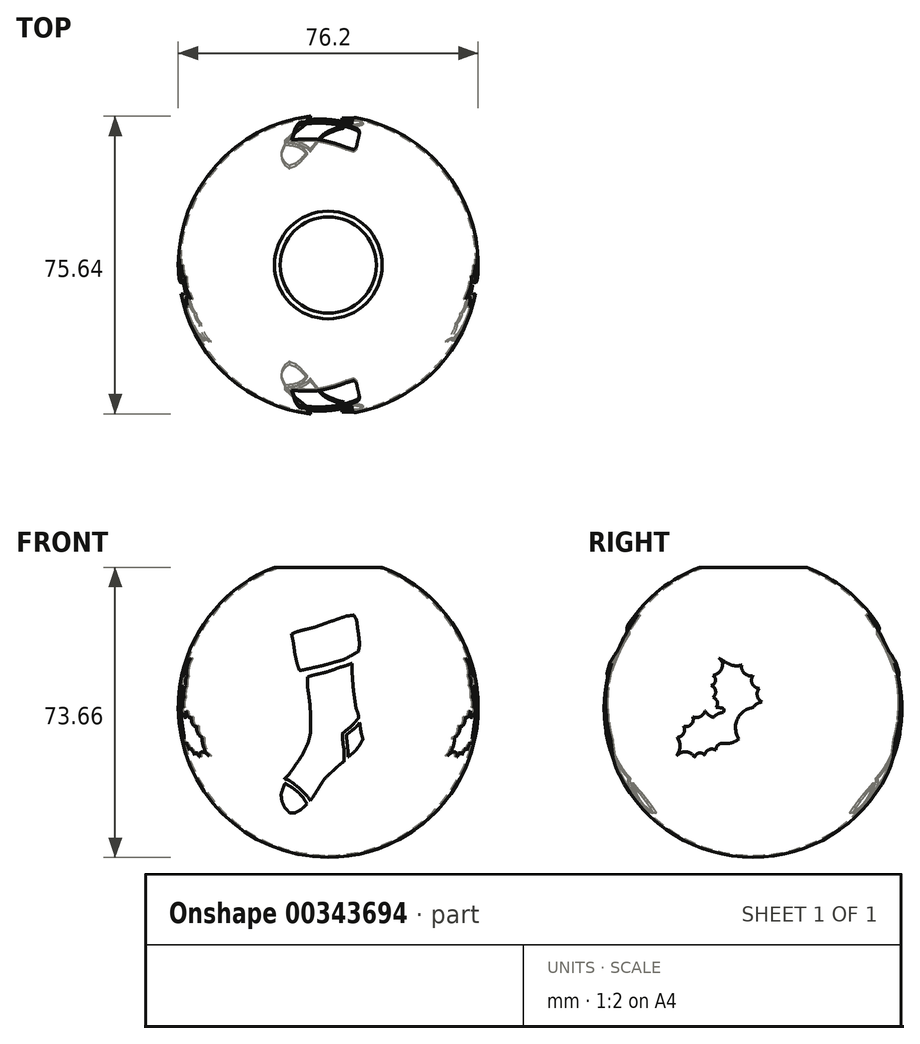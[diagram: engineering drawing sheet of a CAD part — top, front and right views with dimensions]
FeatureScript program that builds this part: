
annotation { "Feature Type Name" : "Feature", "Feature Type Description" : "" }
export const myFeature = defineFeature(function(context is Context, id is Id, definition is map)
    precondition{}
    {
        {
            var Q0;
            Q0=qCreatedBy(makeId("Front.planeOp"),FACE);
            var sketch = newSketch(context, id + "F0", { "sketchPlane" : qUnion([Q0])});
            skArc(sketch, "E0", {"start": v(0, -38.1) * mm, "mid": v(38.1, 0) * mm, "end": v(0, 38.1) * mm});
            skLineSegment(sketch, "E1", {"start": v(0, 38.1) * mm, "end": v(0, -38.1) * mm});
            skSolve(sketch);
        }
        {
            var Q0;
            Q0=makeQuery(id+"F0.imprint","IMPRINT",FACE,{"disambiguationData":[TD([[makeQuery(id+"F0.imprint","IMPRINT",EDGE,{"derivedFrom":sQuery(id+"F0.wireOp",EDGE,"E0")}),1.0]])]});
            var Q1;
            Q1=sQuery(id+"F0.wireOp",EDGE,"E1");
            revolve(context, id + "F1", {"entities" : qUnion([Q0]), "axis" : qUnion([Q1]), "revolveType" : RevolveType.FULL});
        }
        {
            var Q0;
            Q0=qCreatedBy(makeId("Top.planeOp"),FACE);
            cPlane(context, id + "F2", {"entities" : qUnion([Q0]), "cplaneType" : CPlaneType.OFFSET, "offset" : 35.56 * mm, "width" : 152.4 * mm, "height" : 152.4 * mm});
        }
        {
            var Q0;
            Q0=qCreatedBy(id+"F2.planeOp",FACE);
            var sketch = newSketch(context, id + "F3", { "sketchPlane" : qUnion([Q0])});
            skLineSegment(sketch, "E2.bottom", {"start": v(16.51, -16.51) * mm, "end": v(-16.51, -16.51) * mm});
            skLineSegment(sketch, "E2.top", {"start": v(16.5, 16.51) * mm, "end": v(-16.51, 16.51) * mm});
            skLineSegment(sketch, "E2.left", {"start": v(16.51, -16.51) * mm, "end": v(16.5, 16.51) * mm});
            skLineSegment(sketch, "E2.right", {"start": v(-16.51, -16.51) * mm, "end": v(-16.51, 16.51) * mm});
            skPoint(sketch, "E2.middle", {"position": v(0, 0) * mm});
            skSolve(sketch);
        }
        {
            var Q0;
            Q0=makeQuery(id+"F3.imprint","IMPRINT",FACE,{"disambiguationData":[TD([[makeQuery(id+"F3.imprint","IMPRINT",EDGE,{"derivedFrom":sQuery(id+"F3.wireOp",EDGE,"E2.bottom")}),-1.0]])]});
            extrude(context, id + "F4", {"entities" : qUnion([Q0]), "operationType" : NewBodyOperationType.REMOVE, "depth" : 25.4 * mm});
        }
        {
            var Q0;
            Q0=makeQuery(id+"F4.boolean.opBoolean","COPY",FACE,{"derivedFrom":makeQuery(id+"F4.opExtrude","CAP_FACE",FACE,{"disambiguationData":[OSD([sQuery(id+"F3.wireOp",EDGE,"E2.bottom"),sQuery(id+"F3.wireOp",EDGE,"E2.top"),sQuery(id+"F3.wireOp",EDGE,"E2.left"),sQuery(id+"F3.wireOp",EDGE,"E2.right")])],"isStart":true})});
            shell(context, id + "F5", {"entities" : qUnion([Q0]), "thickness" : 0.5 * mm});
        }
        {
            var Q0;
            Q0=qCreatedBy(makeId("Front.planeOp"),FACE);
            var sketch = newSketch(context, id + "F6", { "sketchPlane" : qUnion([Q0])});
            skLineSegment(sketch, "E3.bottom", {"start": v(21.25, -28.37) * mm, "end": v(-21.25, -28.37) * mm});
            skLineSegment(sketch, "E3.top", {"start": v(21.25, 28.37) * mm, "end": v(-21.25, 28.37) * mm});
            skLineSegment(sketch, "E3.left", {"start": v(21.25, -28.37) * mm, "end": v(21.25, 28.37) * mm});
            skLineSegment(sketch, "E3.right", {"start": v(-21.25, -28.37) * mm, "end": v(-21.25, 28.37) * mm});
            skPoint(sketch, "E3.middle", {"position": v(0, 0) * mm});
            skLineSegment(sketch, "E4", {"start": v(7.99, -3.87) * mm, "end": v(7.02, -5.06) * mm});
            skLineSegment(sketch, "E5", {"start": v(7.02, -5.06) * mm, "end": v(5.5, -6.3) * mm});
            skLineSegment(sketch, "E6", {"start": v(5.5, -6.3) * mm, "end": v(4.57, -7) * mm});
            skLineSegment(sketch, "E7", {"start": v(4.57, -7) * mm, "end": v(4.83, -9.38) * mm});
            skLineSegment(sketch, "E8", {"start": v(4.83, -9.38) * mm, "end": v(5.05, -11.5) * mm});
            skLineSegment(sketch, "E9", {"start": v(5.05, -11.5) * mm, "end": v(5.05, -12.65) * mm});
            skLineSegment(sketch, "E10", {"start": v(5.05, -12.65) * mm, "end": v(6.9, -11.03) * mm});
            skLineSegment(sketch, "E11", {"start": v(6.9, -11.03) * mm, "end": v(8.06, -9.46) * mm});
            skLineSegment(sketch, "E12", {"start": v(8.06, -9.46) * mm, "end": v(8.79, -8.1) * mm});
            skLineSegment(sketch, "E13", {"start": v(8.79, -8.1) * mm, "end": v(8.32, -6.34) * mm});
            skLineSegment(sketch, "E14", {"start": v(8.32, -6.34) * mm, "end": v(7.99, -3.87) * mm});
            skLineSegment(sketch, "E15", {"start": v(-11, -19.31) * mm, "end": v(-11.56, -20.72) * mm});
            skLineSegment(sketch, "E16", {"start": v(-11.56, -20.72) * mm, "end": v(-12, -22.15) * mm});
            skLineSegment(sketch, "E17", {"start": v(-12, -22.15) * mm, "end": v(-11.78, -23.85) * mm});
            skLineSegment(sketch, "E18", {"start": v(-11.78, -23.85) * mm, "end": v(-11.1, -25.37) * mm});
            skLineSegment(sketch, "E19", {"start": v(-11.1, -25.37) * mm, "end": v(-9.86, -26.76) * mm});
            skLineSegment(sketch, "E20", {"start": v(-9.86, -26.76) * mm, "end": v(-8.38, -26.76) * mm});
            skLineSegment(sketch, "E21", {"start": v(-8.38, -26.76) * mm, "end": v(-6.94, -26) * mm});
            skLineSegment(sketch, "E22", {"start": v(-6.94, -26) * mm, "end": v(-5.4, -24.55) * mm});
            skLineSegment(sketch, "E23", {"start": v(-5.4, -24.55) * mm, "end": v(-6.29, -23.06) * mm});
            skLineSegment(sketch, "E24", {"start": v(-6.29, -23.06) * mm, "end": v(-7.65, -21.58) * mm});
            skLineSegment(sketch, "E25", {"start": v(-7.65, -21.58) * mm, "end": v(-9.09, -20.42) * mm});
            skLineSegment(sketch, "E26", {"start": v(-9.09, -20.42) * mm, "end": v(-11, -19.31) * mm});
            skLineSegment(sketch, "E27", {"start": v(-9.32, 18.63) * mm, "end": v(-8.83, 16.26) * mm});
            skLineSegment(sketch, "E28", {"start": v(-8.83, 16.26) * mm, "end": v(-8.46, 13.49) * mm});
            skLineSegment(sketch, "E29", {"start": v(-8.46, 13.49) * mm, "end": v(-7.89, 11) * mm});
            skLineSegment(sketch, "E30", {"start": v(-7.89, 11) * mm, "end": v(-7.3, 9.32) * mm});
            skLineSegment(sketch, "E31", {"start": v(-7.3, 9.32) * mm, "end": v(-4.76, 9.87) * mm});
            skLineSegment(sketch, "E32", {"start": v(-4.76, 9.87) * mm, "end": v(-1.13, 10.68) * mm});
            skLineSegment(sketch, "E33", {"start": v(-1.13, 10.68) * mm, "end": v(1.48, 11.45) * mm});
            skLineSegment(sketch, "E34", {"start": v(1.48, 11.45) * mm, "end": v(4.04, 12.17) * mm});
            skLineSegment(sketch, "E35", {"start": v(4.04, 12.17) * mm, "end": v(6.16, 13.36) * mm});
            skLineSegment(sketch, "E36", {"start": v(6.16, 13.36) * mm, "end": v(7.68, 14.21) * mm});
            skLineSegment(sketch, "E37", {"start": v(7.68, 14.21) * mm, "end": v(7.99, 16.24) * mm});
            skLineSegment(sketch, "E38", {"start": v(7.99, 16.24) * mm, "end": v(7.73, 18.19) * mm});
            skLineSegment(sketch, "E39", {"start": v(7.73, 18.19) * mm, "end": v(7.41, 20.54) * mm});
            skLineSegment(sketch, "E40", {"start": v(7.41, 20.54) * mm, "end": v(7.18, 22.24) * mm});
            skLineSegment(sketch, "E41", {"start": v(7.18, 22.24) * mm, "end": v(6.51, 23.43) * mm});
            skLineSegment(sketch, "E42", {"start": v(6.51, 23.43) * mm, "end": v(4.53, 23.16) * mm});
            skLineSegment(sketch, "E43", {"start": v(4.53, 23.16) * mm, "end": v(1.92, 22.28) * mm});
            skLineSegment(sketch, "E44", {"start": v(1.92, 22.28) * mm, "end": v(-1.07, 21.23) * mm});
            skLineSegment(sketch, "E45", {"start": v(-1.07, 21.23) * mm, "end": v(-3.54, 20.32) * mm});
            skLineSegment(sketch, "E46", {"start": v(-3.54, 20.32) * mm, "end": v(-5.98, 19.74) * mm});
            skLineSegment(sketch, "E47", {"start": v(-5.98, 19.74) * mm, "end": v(-7.89, 19.24) * mm});
            skLineSegment(sketch, "E48", {"start": v(-7.89, 19.24) * mm, "end": v(-9.32, 18.63) * mm});
            skLineSegment(sketch, "E49", {"start": v(-11.16, -18.17) * mm, "end": v(-10.25, -18.4) * mm});
            skLineSegment(sketch, "E50", {"start": v(-10.25, -18.4) * mm, "end": v(-9.32, -18.94) * mm});
            skLineSegment(sketch, "E51", {"start": v(-9.32, -18.94) * mm, "end": v(-8.4, -19.68) * mm});
            skLineSegment(sketch, "E52", {"start": v(-8.4, -19.68) * mm, "end": v(-7.26, -20.6) * mm});
            skLineSegment(sketch, "E53", {"start": v(-7.26, -20.6) * mm, "end": v(-6.29, -21.58) * mm});
            skLineSegment(sketch, "E54", {"start": v(-6.29, -21.58) * mm, "end": v(-5.31, -22.56) * mm});
            skLineSegment(sketch, "E55", {"start": v(-5.31, -22.56) * mm, "end": v(-4.54, -23.7) * mm});
            skLineSegment(sketch, "E56", {"start": v(-4.54, -23.7) * mm, "end": v(-3.73, -22.56) * mm});
            skLineSegment(sketch, "E57", {"start": v(-3.73, -22.56) * mm, "end": v(-2.68, -20.89) * mm});
            skLineSegment(sketch, "E58", {"start": v(-2.68, -20.89) * mm, "end": v(-1.88, -19.57) * mm});
            skLineSegment(sketch, "E59", {"start": v(-1.88, -19.57) * mm, "end": v(-0.96, -18.16) * mm});
            skLineSegment(sketch, "E60", {"start": v(-0.96, -18.16) * mm, "end": v(0.25, -16.96) * mm});
            skLineSegment(sketch, "E61", {"start": v(0.25, -16.96) * mm, "end": v(1.32, -16.03) * mm});
            skLineSegment(sketch, "E62", {"start": v(1.32, -16.03) * mm, "end": v(2.34, -15.02) * mm});
            skLineSegment(sketch, "E63", {"start": v(2.34, -15.02) * mm, "end": v(3.5, -14.06) * mm});
            skLineSegment(sketch, "E64", {"start": v(3.5, -14.06) * mm, "end": v(4.06, -13.73) * mm});
            skLineSegment(sketch, "E65", {"start": v(4.06, -13.73) * mm, "end": v(4.06, -12.82) * mm});
            skLineSegment(sketch, "E66", {"start": v(4.06, -12.82) * mm, "end": v(4.06, -11.83) * mm});
            skLineSegment(sketch, "E67", {"start": v(4.06, -11.83) * mm, "end": v(4.06, -10.83) * mm});
            skLineSegment(sketch, "E68", {"start": v(4.06, -10.83) * mm, "end": v(3.83, -9.8) * mm});
            skLineSegment(sketch, "E69", {"start": v(3.83, -9.8) * mm, "end": v(3.67, -8.4) * mm});
            skLineSegment(sketch, "E70", {"start": v(3.67, -8.4) * mm, "end": v(3.56, -6.7) * mm});
            skLineSegment(sketch, "E71", {"start": v(3.56, -6.7) * mm, "end": v(4.57, -5.86) * mm});
            skLineSegment(sketch, "E72", {"start": v(4.57, -5.86) * mm, "end": v(5.67, -4.96) * mm});
            skLineSegment(sketch, "E73", {"start": v(5.67, -4.96) * mm, "end": v(6.5, -4.14) * mm});
            skLineSegment(sketch, "E74", {"start": v(6.5, -4.14) * mm, "end": v(7.35, -3.1) * mm});
            skLineSegment(sketch, "E75", {"start": v(7.35, -3.1) * mm, "end": v(7.76, -2.7) * mm});
            skLineSegment(sketch, "E76", {"start": v(7.76, -2.7) * mm, "end": v(7.56, -1.48) * mm});
            skLineSegment(sketch, "E77", {"start": v(7.56, -1.48) * mm, "end": v(7.05, -0.23) * mm});
            skLineSegment(sketch, "E78", {"start": v(7.05, -0.23) * mm, "end": v(6.79, 1.54) * mm});
            skLineSegment(sketch, "E79", {"start": v(6.79, 1.54) * mm, "end": v(6.56, 3.12) * mm});
            skLineSegment(sketch, "E80", {"start": v(6.56, 3.12) * mm, "end": v(6.31, 5.1) * mm});
            skLineSegment(sketch, "E81", {"start": v(6.31, 5.1) * mm, "end": v(6.18, 7.12) * mm});
            skLineSegment(sketch, "E82", {"start": v(6.18, 7.12) * mm, "end": v(6.06, 8.96) * mm});
            skLineSegment(sketch, "E83", {"start": v(6.06, 8.96) * mm, "end": v(6.06, 10.5) * mm});
            skLineSegment(sketch, "E84", {"start": v(6.06, 10.5) * mm, "end": v(6.01, 11.18) * mm});
            skLineSegment(sketch, "E85", {"start": v(6.01, 11.18) * mm, "end": v(4.57, 10.62) * mm});
            skLineSegment(sketch, "E86", {"start": v(4.57, 10.62) * mm, "end": v(2.81, 10.15) * mm});
            skLineSegment(sketch, "E87", {"start": v(2.81, 10.15) * mm, "end": v(1.27, 9.54) * mm});
            skLineSegment(sketch, "E88", {"start": v(1.27, 9.54) * mm, "end": v(-0.71, 8.9) * mm});
            skLineSegment(sketch, "E89", {"start": v(-0.71, 8.9) * mm, "end": v(-2.53, 8.46) * mm});
            skLineSegment(sketch, "E90", {"start": v(-2.53, 8.46) * mm, "end": v(-4.16, 8.1) * mm});
            skLineSegment(sketch, "E91", {"start": v(-4.16, 8.1) * mm, "end": v(-5.31, 7.72) * mm});
            skLineSegment(sketch, "E92", {"start": v(-5.31, 7.72) * mm, "end": v(-5.31, 6.24) * mm});
            skLineSegment(sketch, "E93", {"start": v(-5.31, 6.24) * mm, "end": v(-5.22, 4.9) * mm});
            skLineSegment(sketch, "E94", {"start": v(-5.22, 4.9) * mm, "end": v(-4.92, 2.96) * mm});
            skLineSegment(sketch, "E95", {"start": v(-4.92, 2.96) * mm, "end": v(-4.67, 0.9) * mm});
            skLineSegment(sketch, "E96", {"start": v(-4.67, 0.9) * mm, "end": v(-4.55, -0.96) * mm});
            skLineSegment(sketch, "E97", {"start": v(-4.55, -0.96) * mm, "end": v(-4.55, -3.08) * mm});
            skLineSegment(sketch, "E98", {"start": v(-4.55, -3.08) * mm, "end": v(-4.55, -4.42) * mm});
            skLineSegment(sketch, "E99", {"start": v(-4.55, -4.42) * mm, "end": v(-4.55, -6.7) * mm});
            skLineSegment(sketch, "E100", {"start": v(-4.55, -6.7) * mm, "end": v(-5.03, -8.73) * mm});
            skLineSegment(sketch, "E101", {"start": v(-5.03, -8.73) * mm, "end": v(-5.65, -10.16) * mm});
            skLineSegment(sketch, "E102", {"start": v(-5.65, -10.16) * mm, "end": v(-6.5, -11.91) * mm});
            skLineSegment(sketch, "E103", {"start": v(-6.5, -11.91) * mm, "end": v(-7.37, -13.3) * mm});
            skLineSegment(sketch, "E104", {"start": v(-7.37, -13.3) * mm, "end": v(-8.16, -14.42) * mm});
            skLineSegment(sketch, "E105", {"start": v(-8.16, -14.42) * mm, "end": v(-9.16, -15.9) * mm});
            skLineSegment(sketch, "E106", {"start": v(-9.16, -15.9) * mm, "end": v(-10.1, -17.22) * mm});
            skLineSegment(sketch, "E107", {"start": v(-10.1, -17.22) * mm, "end": v(-11.16, -18.17) * mm});
            skArc(sketch, "E108", {"start": v(8.32, 23.55) * mm, "mid": v(7.94, 24.06) * mm, "end": v(7.37, 24.35) * mm});
            skLineSegment(sketch, "E109", {"start": v(8.32, 23.55) * mm, "end": v(8.48, 22.17) * mm});
            skLineSegment(sketch, "E110", {"start": v(8.48, 22.17) * mm, "end": v(8.6, 20.99) * mm});
            skLineSegment(sketch, "E111", {"start": v(8.6, 20.99) * mm, "end": v(8.72, 19.86) * mm});
            skLineSegment(sketch, "E112", {"start": v(8.72, 19.86) * mm, "end": v(9.04, 18.6) * mm});
            skLineSegment(sketch, "E113", {"start": v(9.04, 18.6) * mm, "end": v(9.24, 17.76) * mm});
            skLineSegment(sketch, "E114", {"start": v(9.24, 17.76) * mm, "end": v(9.24, 17.4) * mm});
            skLineSegment(sketch, "E115", {"start": v(9.24, 17.4) * mm, "end": v(9.24, 15.65) * mm});
            skArc(sketch, "E116", {"start": v(9.05, 14.16) * mm, "mid": v(9.19, 14.9) * mm, "end": v(9.24, 15.65) * mm});
            skLineSegment(sketch, "E117", {"start": v(9.05, 14.16) * mm, "end": v(8.16, 13.16) * mm});
            skLineSegment(sketch, "E118", {"start": v(8.16, 13.16) * mm, "end": v(7.24, 12.32) * mm});
            skLineSegment(sketch, "E119", {"start": v(7.24, 12.32) * mm, "end": v(7.24, 11.36) * mm});
            skLineSegment(sketch, "E120", {"start": v(7.24, 11.36) * mm, "end": v(7.24, 10.37) * mm});
            skLineSegment(sketch, "E121", {"start": v(7.24, 10.37) * mm, "end": v(7.24, 8.7) * mm});
            skLineSegment(sketch, "E122", {"start": v(7.24, 8.7) * mm, "end": v(7.24, 6.82) * mm});
            skLineSegment(sketch, "E123", {"start": v(7.24, 6.82) * mm, "end": v(7.45, 5.06) * mm});
            skLineSegment(sketch, "E124", {"start": v(7.45, 5.06) * mm, "end": v(7.58, 3.41) * mm});
            skLineSegment(sketch, "E125", {"start": v(7.58, 3.41) * mm, "end": v(7.79, 1.83) * mm});
            skLineSegment(sketch, "E126", {"start": v(7.79, 1.83) * mm, "end": v(8.04, 0.59) * mm});
            skLineSegment(sketch, "E127", {"start": v(8.04, 0.59) * mm, "end": v(8.39, -0.63) * mm});
            skLineSegment(sketch, "E128", {"start": v(8.39, -0.63) * mm, "end": v(8.78, -2.4) * mm});
            skLineSegment(sketch, "E129", {"start": v(8.78, -2.4) * mm, "end": v(9.05, -4.12) * mm});
            skArc(sketch, "E130", {"start": v(9.34, -6.35) * mm, "mid": v(9.21, -5.23) * mm, "end": v(9.05, -4.12) * mm});
            skLineSegment(sketch, "E131", {"start": v(9.34, -6.35) * mm, "end": v(9.6, -7.11) * mm});
            skLineSegment(sketch, "E132", {"start": v(9.6, -7.11) * mm, "end": v(9.7, -8.48) * mm});
            skLineSegment(sketch, "E133", {"start": v(9.7, -8.48) * mm, "end": v(9.34, -9.46) * mm});
            skLineSegment(sketch, "E134", {"start": v(9.34, -9.46) * mm, "end": v(8.64, -10.56) * mm});
            skLineSegment(sketch, "E135", {"start": v(8.64, -10.56) * mm, "end": v(7.74, -11.75) * mm});
            skLineSegment(sketch, "E136", {"start": v(7.74, -11.75) * mm, "end": v(6.73, -12.87) * mm});
            skLineSegment(sketch, "E137", {"start": v(6.73, -12.87) * mm, "end": v(5.95, -13.44) * mm});
            skLineSegment(sketch, "E138", {"start": v(5.95, -13.44) * mm, "end": v(5.1, -14.04) * mm});
            skLineSegment(sketch, "E139", {"start": v(5.1, -14.04) * mm, "end": v(3.97, -14.94) * mm});
            skLineSegment(sketch, "E140", {"start": v(3.97, -14.94) * mm, "end": v(2.78, -16.07) * mm});
            skLineSegment(sketch, "E141", {"start": v(2.78, -16.07) * mm, "end": v(1.96, -16.92) * mm});
            skLineSegment(sketch, "E142", {"start": v(1.96, -16.92) * mm, "end": v(0.81, -18.09) * mm});
            skLineSegment(sketch, "E143", {"start": v(0.81, -18.09) * mm, "end": v(0, -19.12) * mm});
            skLineSegment(sketch, "E144", {"start": v(0, -19.12) * mm, "end": v(-1.09, -20.6) * mm});
            skLineSegment(sketch, "E145", {"start": v(-1.09, -20.6) * mm, "end": v(-2.08, -22.03) * mm});
            skLineSegment(sketch, "E146", {"start": v(-2.08, -22.03) * mm, "end": v(-2.98, -23.41) * mm});
            skLineSegment(sketch, "E147", {"start": v(-2.98, -23.41) * mm, "end": v(-3.62, -24.4) * mm});
            skLineSegment(sketch, "E148", {"start": v(-3.62, -24.4) * mm, "end": v(-4.56, -25.47) * mm});
            skLineSegment(sketch, "E149", {"start": v(-4.56, -25.47) * mm, "end": v(-5.79, -26.54) * mm});
            skLineSegment(sketch, "E150", {"start": v(-5.79, -26.54) * mm, "end": v(-7.17, -27.47) * mm});
            skLineSegment(sketch, "E151", {"start": v(-7.17, -27.47) * mm, "end": v(-8.2, -27.96) * mm});
            skLineSegment(sketch, "E152", {"start": v(-8.2, -27.96) * mm, "end": v(-9.56, -27.96) * mm});
            skLineSegment(sketch, "E153", {"start": v(-9.56, -27.96) * mm, "end": v(-10.73, -27.52) * mm});
            skLineSegment(sketch, "E154", {"start": v(-10.73, -27.52) * mm, "end": v(-11.6, -26.65) * mm});
            skLineSegment(sketch, "E155", {"start": v(-11.6, -26.65) * mm, "end": v(-12.3, -25.32) * mm});
            skLineSegment(sketch, "E156", {"start": v(-12.3, -25.32) * mm, "end": v(-12.92, -23.83) * mm});
            skLineSegment(sketch, "E157", {"start": v(-12.92, -23.83) * mm, "end": v(-13.17, -22.99) * mm});
            skLineSegment(sketch, "E158", {"start": v(-13.17, -22.99) * mm, "end": v(-13.17, -21.98) * mm});
            skLineSegment(sketch, "E159", {"start": v(-13.17, -21.98) * mm, "end": v(-13.17, -20.9) * mm});
            skLineSegment(sketch, "E160", {"start": v(-13.17, -20.9) * mm, "end": v(-12.9, -20.03) * mm});
            skLineSegment(sketch, "E161", {"start": v(-12.9, -20.03) * mm, "end": v(-12.5, -19.15) * mm});
            skLineSegment(sketch, "E162", {"start": v(-12.5, -19.15) * mm, "end": v(-12.05, -18.1) * mm});
            skLineSegment(sketch, "E163", {"start": v(-12.05, -18.1) * mm, "end": v(-11.43, -16.92) * mm});
            skLineSegment(sketch, "E164", {"start": v(-11.43, -16.92) * mm, "end": v(-10.87, -16.05) * mm});
            skLineSegment(sketch, "E165", {"start": v(-10.87, -16.05) * mm, "end": v(-10, -14.88) * mm});
            skLineSegment(sketch, "E166", {"start": v(-10, -14.88) * mm, "end": v(-9.4, -13.83) * mm});
            skLineSegment(sketch, "E167", {"start": v(-9.4, -13.83) * mm, "end": v(-8.57, -12.66) * mm});
            skLineSegment(sketch, "E168", {"start": v(-8.57, -12.66) * mm, "end": v(-7.8, -11.58) * mm});
            skLineSegment(sketch, "E169", {"start": v(-7.8, -11.58) * mm, "end": v(-7.22, -10.6) * mm});
            skLineSegment(sketch, "E170", {"start": v(-7.22, -10.6) * mm, "end": v(-6.68, -9.25) * mm});
            skLineSegment(sketch, "E171", {"start": v(-6.68, -9.25) * mm, "end": v(-6.06, -7.87) * mm});
            skLineSegment(sketch, "E172", {"start": v(-6.06, -7.87) * mm, "end": v(-5.87, -6.75) * mm});
            skLineSegment(sketch, "E173", {"start": v(-5.87, -6.75) * mm, "end": v(-5.76, -4.73) * mm});
            skLineSegment(sketch, "E174", {"start": v(-5.76, -4.73) * mm, "end": v(-5.63, -3.24) * mm});
            skLineSegment(sketch, "E175", {"start": v(-5.63, -3.24) * mm, "end": v(-5.63, -2.13) * mm});
            skLineSegment(sketch, "E176", {"start": v(-5.63, -2.13) * mm, "end": v(-5.87, -0.7) * mm});
            skLineSegment(sketch, "E177", {"start": v(-5.87, -0.7) * mm, "end": v(-6.06, 1.08) * mm});
            skLineSegment(sketch, "E178", {"start": v(-6.06, 1.08) * mm, "end": v(-6.14, 2.27) * mm});
            skLineSegment(sketch, "E179", {"start": v(-6.14, 2.27) * mm, "end": v(-6.41, 4.27) * mm});
            skLineSegment(sketch, "E180", {"start": v(-6.41, 4.27) * mm, "end": v(-6.5, 6.08) * mm});
            skLineSegment(sketch, "E181", {"start": v(-6.5, 6.08) * mm, "end": v(-6.65, 7.84) * mm});
            skLineSegment(sketch, "E182", {"start": v(-6.65, 7.84) * mm, "end": v(-7.66, 7.96) * mm});
            skArc(sketch, "E183", {"start": v(-8.53, 8.67) * mm, "mid": v(-8.2, 8.2) * mm, "end": v(-7.66, 7.96) * mm});
            skLineSegment(sketch, "E184", {"start": v(-8.53, 8.67) * mm, "end": v(-9, 10.08) * mm});
            skLineSegment(sketch, "E185", {"start": v(-9, 10.08) * mm, "end": v(-9, 10.79) * mm});
            skLineSegment(sketch, "E186", {"start": v(-9, 10.79) * mm, "end": v(-9.46, 11.42) * mm});
            skLineSegment(sketch, "E187", {"start": v(-9.46, 11.42) * mm, "end": v(-9.76, 12.62) * mm});
            skLineSegment(sketch, "E188", {"start": v(-9.76, 12.62) * mm, "end": v(-9.97, 13.74) * mm});
            skLineSegment(sketch, "E189", {"start": v(-9.97, 13.74) * mm, "end": v(-10, 14.91) * mm});
            skLineSegment(sketch, "E190", {"start": v(-10, 14.91) * mm, "end": v(-10.38, 16.38) * mm});
            skLineSegment(sketch, "E191", {"start": v(-10.38, 16.38) * mm, "end": v(-10.65, 17.72) * mm});
            skLineSegment(sketch, "E192", {"start": v(-10.65, 17.72) * mm, "end": v(-10.83, 18.55) * mm});
            skLineSegment(sketch, "E193", {"start": v(-10.83, 18.55) * mm, "end": v(-10.4, 19.3) * mm});
            skLineSegment(sketch, "E194", {"start": v(-10.4, 19.3) * mm, "end": v(-9.35, 19.94) * mm});
            skLineSegment(sketch, "E195", {"start": v(-9.35, 19.94) * mm, "end": v(-8.2, 20.45) * mm});
            skLineSegment(sketch, "E196", {"start": v(-8.2, 20.45) * mm, "end": v(-6.9, 20.93) * mm});
            skLineSegment(sketch, "E197", {"start": v(-6.9, 20.93) * mm, "end": v(-5.82, 21.38) * mm});
            skLineSegment(sketch, "E198", {"start": v(-5.82, 21.38) * mm, "end": v(-4.18, 21.96) * mm});
            skLineSegment(sketch, "E199", {"start": v(-4.18, 21.96) * mm, "end": v(-3.14, 22.31) * mm});
            skLineSegment(sketch, "E200", {"start": v(-3.14, 22.31) * mm, "end": v(-2.02, 22.59) * mm});
            skLineSegment(sketch, "E201", {"start": v(-2.02, 22.59) * mm, "end": v(-0.68, 23.02) * mm});
            skLineSegment(sketch, "E202", {"start": v(-0.68, 23.02) * mm, "end": v(0.8, 23.5) * mm});
            skLineSegment(sketch, "E203", {"start": v(0.8, 23.5) * mm, "end": v(2.2, 23.91) * mm});
            skLineSegment(sketch, "E204", {"start": v(2.2, 23.91) * mm, "end": v(2.74, 23.91) * mm});
            skLineSegment(sketch, "E205", {"start": v(2.74, 23.91) * mm, "end": v(3.75, 24.5) * mm});
            skLineSegment(sketch, "E206", {"start": v(3.75, 24.5) * mm, "end": v(4.35, 24.7) * mm});
            skLineSegment(sketch, "E207", {"start": v(4.35, 24.7) * mm, "end": v(5.25, 24.56) * mm});
            skLineSegment(sketch, "E208", {"start": v(5.25, 24.56) * mm, "end": v(7.37, 24.35) * mm});
            skSolve(sketch);
        }
        {
            var Q0;
            Q0=makeQuery(id+"F6.imprint","IMPRINT",FACE,{"disambiguationData":[TD([[makeQuery(id+"F6.imprint","IMPRINT",EDGE,{"derivedFrom":sQuery(id+"F6.wireOp",EDGE,"E27")}),1.0]])]});
            var Q1;
            Q1=makeQuery(id+"F6.imprint","IMPRINT",FACE,{"disambiguationData":[TD([[makeQuery(id+"F6.imprint","IMPRINT",EDGE,{"derivedFrom":sQuery(id+"F6.wireOp",EDGE,"E49")}),1.0]])]});
            var Q2;
            Q2=makeQuery(id+"F6.imprint","IMPRINT",FACE,{"disambiguationData":[TD([[makeQuery(id+"F6.imprint","IMPRINT",EDGE,{"derivedFrom":sQuery(id+"F6.wireOp",EDGE,"E4")}),1.0]])]});
            var Q3;
            Q3=makeQuery(id+"F6.imprint","IMPRINT",FACE,{"disambiguationData":[TD([[makeQuery(id+"F6.imprint","IMPRINT",EDGE,{"derivedFrom":sQuery(id+"F6.wireOp",EDGE,"E15")}),1.0]])]});
            extrude(context, id + "F7", {"entities" : qUnion([Q0, Q1, Q2, Q3]), "operationType" : NewBodyOperationType.REMOVE, "endBound" : BoundingType.SYMMETRIC, "oppositeDirection" : true, "depth" : 77.72 * mm});
        }
        {
            var Q0;
            Q0=qCreatedBy(makeId("Right.planeOp"),FACE);
            var sketch = newSketch(context, id + "F8", { "sketchPlane" : qUnion([Q0])});
            skLineSegment(sketch, "E209.bottom", {"start": v(21.4, -14.5) * mm, "end": v(-21.4, -14.5) * mm});
            skLineSegment(sketch, "E209.top", {"start": v(21.4, 14.5) * mm, "end": v(-21.4, 14.5) * mm});
            skLineSegment(sketch, "E209.left", {"start": v(21.4, -14.5) * mm, "end": v(21.4, 14.5) * mm});
            skLineSegment(sketch, "E209.right", {"start": v(-21.4, -14.5) * mm, "end": v(-21.4, 14.5) * mm});
            skPoint(sketch, "E209.middle", {"position": v(0, 0) * mm});
            skArc(sketch, "E210", {"start": v(-7, 11.56) * mm, "mid": v(-5.05, 10.64) * mm, "end": v(-2.88, 10.75) * mm});
            skArc(sketch, "E211", {"start": v(-2.88, 10.75) * mm, "mid": v(-2.18, 8.62) * mm, "end": v(0, 8.09) * mm});
            skArc(sketch, "E212", {"start": v(0, 8.09) * mm, "mid": v(-0.2, 5.99) * mm, "end": v(1.56, 4.82) * mm});
            skArc(sketch, "E213", {"start": v(1.56, 4.82) * mm, "mid": v(1.08, 2.92) * mm, "end": v(2.31, 1.39) * mm});
            skArc(sketch, "E214", {"start": v(2.31, 1.39) * mm, "mid": v(1.03, 0.9) * mm, "end": v(0, 0) * mm});
            skArc(sketch, "E215", {"start": v(-10.24, 8.09) * mm, "mid": v(-8.38, 9.22) * mm, "end": v(-7.7, 11.29) * mm});
            skArc(sketch, "E216", {"start": v(-10.74, 5.58) * mm, "mid": v(-9.55, 6.65) * mm, "end": v(-10.24, 8.09) * mm});
            skArc(sketch, "E217", {"start": v(-10.24, 2.51) * mm, "mid": v(-9.5, 4.2) * mm, "end": v(-10.74, 5.58) * mm});
            skArc(sketch, "E218", {"start": v(-9.39, 0) * mm, "mid": v(-9.1, 1.5) * mm, "end": v(-10.24, 2.51) * mm});
            skArc(sketch, "E219", {"start": v(-7.58, -0.23) * mm, "mid": v(-8.48, -0.08) * mm, "end": v(-9.39, 0) * mm});
            skArc(sketch, "E220", {"start": v(-7.7, 11.29) * mm, "mid": v(-8.14, 11.9) * mm, "end": v(-8.64, 12.47) * mm});
            skLineSegment(sketch, "E221", {"start": v(-8.64, 12.47) * mm, "end": v(-7, 11.56) * mm});
            skArc(sketch, "E222", {"start": v(0, 0) * mm, "mid": v(-3.88, 2.94) * mm, "end": v(-7.58, -0.23) * mm});
            skArc(sketch, "E223", {"start": v(-3.62, -7.97) * mm, "mid": v(-1.5, -9.25) * mm, "end": v(0.93, -9.78) * mm});
            skArc(sketch, "E224", {"start": v(-7.58, -9.1) * mm, "mid": v(-5.46, -9.03) * mm, "end": v(-3.62, -7.97) * mm});
            skArc(sketch, "E225", {"start": v(-7.58, -1.27) * mm, "mid": v(-11.08, -5.19) * mm, "end": v(-7.58, -9.1) * mm});
            skArc(sketch, "E226", {"start": v(-7.58, -1.27) * mm, "mid": v(-7.38, -0.75) * mm, "end": v(-7.58, -0.23) * mm});
            skArc(sketch, "E227", {"start": v(0, 0) * mm, "mid": v(-3.99, -3) * mm, "end": v(-3.62, -7.97) * mm});
            skArc(sketch, "E228", {"start": v(-3.62, -2.32) * mm, "mid": v(-5.48, -1.37) * mm, "end": v(-7.58, -1.27) * mm});
            skArc(sketch, "E229", {"start": v(3.42, 1.63) * mm, "mid": v(4.92, 1.08) * mm, "end": v(6.14, 2.13) * mm});
            skArc(sketch, "E230", {"start": v(6.14, 2.13) * mm, "mid": v(7.62, 1.16) * mm, "end": v(9.2, 1.95) * mm});
            skArc(sketch, "E231", {"start": v(9.2, 1.95) * mm, "mid": v(10.12, 0.93) * mm, "end": v(11.44, 1.32) * mm});
            skArc(sketch, "E232", {"start": v(11.44, 1.32) * mm, "mid": v(13.04, -0.6) * mm, "end": v(15.53, -0.44) * mm});
            skArc(sketch, "E233", {"start": v(15.53, -0.44) * mm, "mid": v(13.93, -2.26) * mm, "end": v(13.28, -4.6) * mm});
            skArc(sketch, "E234", {"start": v(13.28, -4.6) * mm, "mid": v(11.4, -4.76) * mm, "end": v(10.5, -6.44) * mm});
            skArc(sketch, "E235", {"start": v(10.5, -6.44) * mm, "mid": v(8.63, -6.07) * mm, "end": v(7.34, -7.46) * mm});
            skArc(sketch, "E236", {"start": v(7.34, -7.46) * mm, "mid": v(6.62, -7) * mm, "end": v(5.8, -6.76) * mm});
            skArc(sketch, "E237", {"start": v(3.18, -0.24) * mm, "mid": v(3.47, 0.67) * mm, "end": v(3.42, 1.63) * mm});
            skArc(sketch, "E238", {"start": v(-7.24, -9.16) * mm, "mid": v(-8.76, -9.47) * mm, "end": v(-9.46, -10.86) * mm});
            skArc(sketch, "E239", {"start": v(-9.46, -10.86) * mm, "mid": v(-11.22, -10.75) * mm, "end": v(-12.32, -12.14) * mm});
            skArc(sketch, "E240", {"start": v(-12.32, -12.14) * mm, "mid": v(-13.73, -11.6) * mm, "end": v(-14.84, -12.62) * mm});
            skArc(sketch, "E241", {"start": v(-14.84, -12.62) * mm, "mid": v(-17.1, -11.31) * mm, "end": v(-19.5, -12.34) * mm});
            skArc(sketch, "E242", {"start": v(-19.5, -12.34) * mm, "mid": v(-18.57, -10) * mm, "end": v(-19.27, -7.59) * mm});
            skArc(sketch, "E243", {"start": v(-19.27, -7.59) * mm, "mid": v(-17.63, -6.64) * mm, "end": v(-17.67, -4.75) * mm});
            skArc(sketch, "E244", {"start": v(-17.67, -4.75) * mm, "mid": v(-15.72, -4.35) * mm, "end": v(-15.3, -2.4) * mm});
            skArc(sketch, "E245", {"start": v(-15.3, -2.4) * mm, "mid": v(-13.39, -2.35) * mm, "end": v(-12.2, -0.84) * mm});
            skArc(sketch, "E246", {"start": v(-12.2, -0.84) * mm, "mid": v(-11.3, -1.9) * mm, "end": v(-10.05, -2.53) * mm});
            skSolve(sketch);
        }
        {
            var Q0;
            Q0=makeQuery(id+"F8.imprint","IMPRINT",FACE,{"disambiguationData":[TD([[makeQuery(id+"F8.imprint","IMPRINT",EDGE,{"derivedFrom":sQuery(id+"F8.wireOp",EDGE,"E210")}),-1.0]])]});
            var Q1;
            {var subQ0=sQuery(id+"F8.wireOp",EDGE,"E222");Q1=makeQuery(id+"F8.imprint","IMPRINT",FACE,{"disambiguationData":[TD([[makeQuery(id+"F8.imprint","IMPRINT",EDGE,{"derivedFrom":subQ0}),1.0]])]});}
            var Q2;
            {var subQ4=sQuery(id+"F8.wireOp",EDGE,"E228");Q2=makeQuery(id+"F8.imprint","IMPRINT",FACE,{"disambiguationData":[TD([[makeQuery(id+"F8.imprint","IMPRINT",EDGE,{"derivedFrom":subQ4}),1.0]])]});}
            var Q3;
            {var subQ0=sQuery(id+"F8.wireOp",EDGE,"E223");Q3=makeQuery(id+"F8.imprint","IMPRINT",FACE,{"disambiguationData":[TD([[makeQuery(id+"F8.imprint","IMPRINT",EDGE,{"derivedFrom":subQ0}),1.0]])]});}
            var Q4;
            Q4=makeQuery(id+"F8.imprint","IMPRINT",FACE,{"disambiguationData":[TD([[makeQuery(id+"F8.imprint","IMPRINT",EDGE,{"derivedFrom":sQuery(id+"F8.wireOp",EDGE,"E229")}),-1.0]])]});
            var Q5;
            {var subQ8=sQuery(id+"F8.wireOp",EDGE,"E239");Q5=makeQuery(id+"F8.imprint","IMPRINT",FACE,{"disambiguationData":[TD([[makeQuery(id+"F8.imprint","IMPRINT",EDGE,{"derivedFrom":subQ8}),-1.0]])]});}
            extrude(context, id + "F9", {"entities" : qUnion([Q0, Q1, Q2, Q3, Q4, Q5]), "operationType" : NewBodyOperationType.REMOVE, "endBound" : BoundingType.SYMMETRIC, "depth" : 77.72 * mm});
        }
    });
